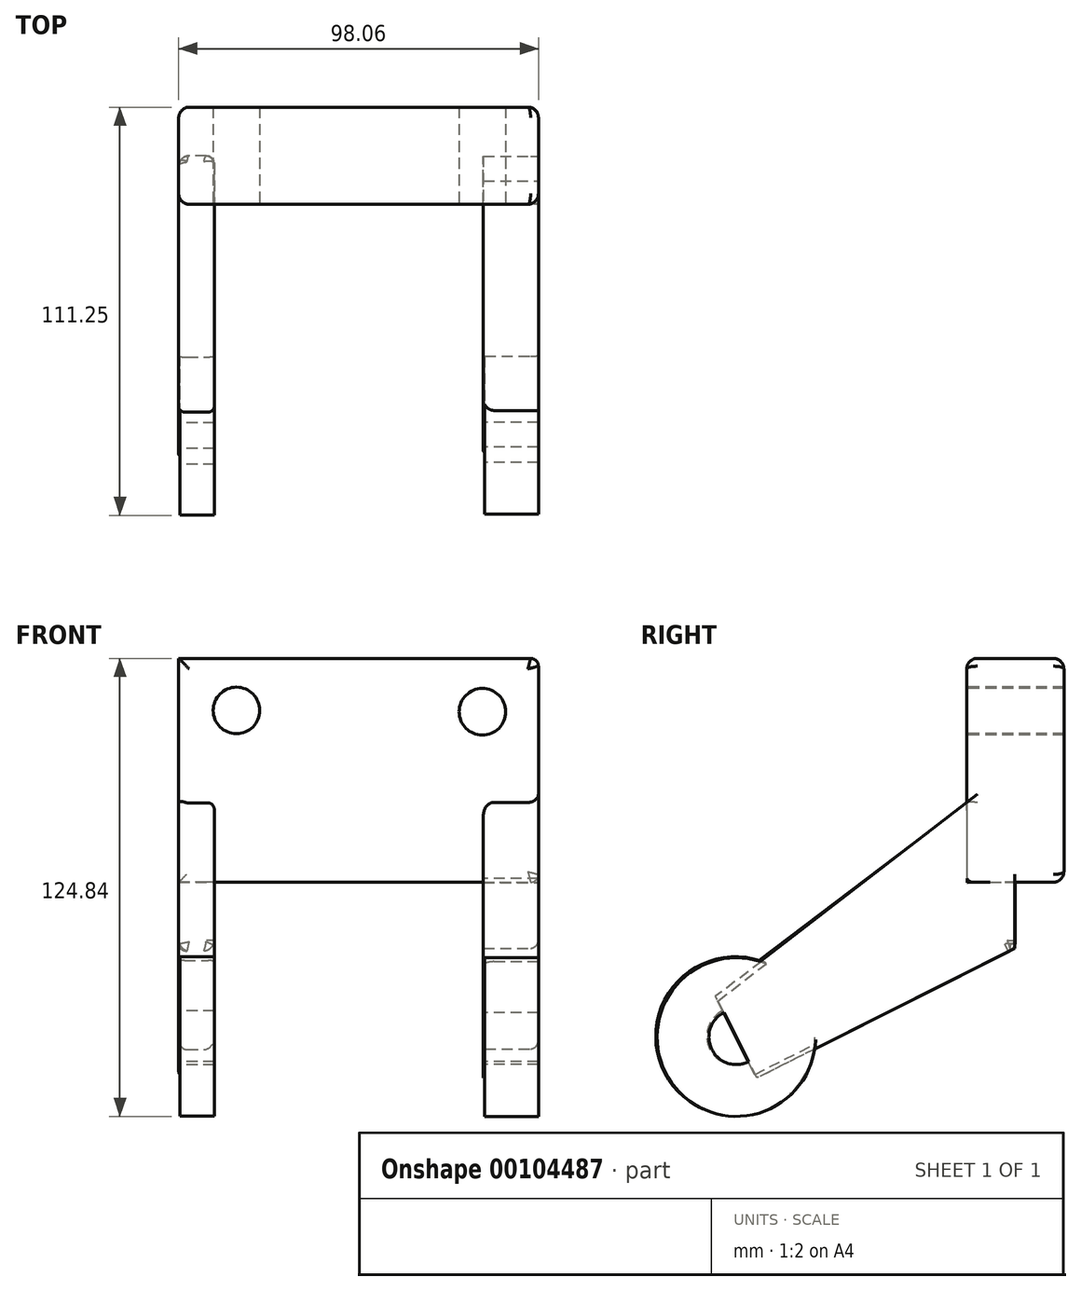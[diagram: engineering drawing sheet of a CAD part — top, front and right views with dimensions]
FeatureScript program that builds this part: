
annotation { "Feature Type Name" : "Feature", "Feature Type Description" : "" }
export const myFeature = defineFeature(function(context is Context, id is Id, definition is map)
    precondition{}
    {
        {
            var Q0;
            Q0=qCreatedBy(makeId("Front.planeOp"),FACE);
            var sketch = newSketch(context, id + "F0", { "sketchPlane" : qUnion([Q0])});
            skLineSegment(sketch, "E0.bottom", {"start": v(-42.16, 33.22) * mm, "end": v(55.9, 33.22) * mm});
            skLineSegment(sketch, "E0.top", {"start": v(-42.16, -27.8) * mm, "end": v(55.9, -27.8) * mm});
            skLineSegment(sketch, "E0.left", {"start": v(-42.16, 33.22) * mm, "end": v(-42.16, -27.8) * mm});
            skLineSegment(sketch, "E0.right", {"start": v(55.9, 33.22) * mm, "end": v(55.9, -27.8) * mm});
            skSolve(sketch);
        }
        {
            var Q0;
            Q0=qSketchRegion(id+"F0",true);
            var Q1;
            Q1=makeQuery(id+"F0.imprint","IMPRINT",FACE,{"disambiguationData":[TD([[makeQuery(id+"F0.imprint","IMPRINT",EDGE,{"derivedFrom":sQuery(id+"F0.wireOp",EDGE,"E0.bottom")}),-1.0]])]});
            extrude(context, id + "F1", {"entities" : qUnion([Q0, Q1]), "depth" : 26.48 * mm});
        }
        {
            var Q0;
            Q0=makeQuery(id+"F1.opExtrude","CAP_FACE",FACE,{"disambiguationData":[OSD([sQuery(id+"F0.wireOp",EDGE,"E0.bottom"),sQuery(id+"F0.wireOp",EDGE,"E0.top"),sQuery(id+"F0.wireOp",EDGE,"E0.left"),sQuery(id+"F0.wireOp",EDGE,"E0.right")])],"isStart":false});
            var sketch = newSketch(context, id + "F2", { "sketchPlane" : qUnion([Q0])});
            skCircle(sketch, "E1", {"center": v(-26.41, 19.02) * mm, "radius": 5.97 * mm});
            skCircle(sketch, "E2", {"center": v(40.64, 18.66) * mm, "radius": 6.46 * mm});
            skSolve(sketch);
        }
        {
            var Q0;
            Q0=sQuery(id+"F2.wireOp",VERTEX,"E1.center");
            var Q1;
            Q1=sQuery(id+"F2.wireOp",VERTEX,"E2.center");
            var Q2;
            Q2=makeQuery(id+"F1.opExtrude","SWEPT_BODY",BODY,{"disambiguationData":[OSD([sQuery(id+"F0.wireOp",EDGE,"E0.bottom"),sQuery(id+"F0.wireOp",EDGE,"E0.top"),sQuery(id+"F0.wireOp",EDGE,"E0.left"),sQuery(id+"F0.wireOp",EDGE,"E0.right")])]});
            hole(context, id + "F3", {"style" : HoleStyle.SIMPLE, "endStyle" : HoleEndStyle.THROUGH, "holeDiameter" : 12.7 * mm, "locations" : qUnion([Q0, Q1]), "scope" : qUnion([Q2]), "isTappedThrough" : true});
        }
        {
            var Q0;
            Q0=makeQuery(id+"F1.opExtrude","SWEPT_FACE",FACE,{"disambiguationData":[OSD([sQuery(id+"F0.wireOp",EDGE,"E0.right")])]});
            var sketch = newSketch(context, id + "F4", { "sketchPlane" : qUnion([Q0])});
            skSolve(sketch);
        }
        {
            var Q0;
            Q0=makeQuery(id+"F1.opExtrude","SWEPT_FACE",FACE,{"disambiguationData":[OSD([sQuery(id+"F0.wireOp",EDGE,"E0.left")])]});
            var sketch = newSketch(context, id + "F5", { "sketchPlane" : qUnion([Q0])});
            skLineSegment(sketch, "E3", {"start": v(13.24, -27.8) * mm, "end": v(13.24, -45.74) * mm});
            skLineSegment(sketch, "E4", {"start": v(13.24, -45.74) * mm, "end": v(83.77, -81.27) * mm});
            skLineSegment(sketch, "E5", {"start": v(83.77, -81.27) * mm, "end": v(95.33, -58.32) * mm});
            skLineSegment(sketch, "E6", {"start": v(95.33, -58.32) * mm, "end": v(26.48, -6.2) * mm});
            skLineSegment(sketch, "E7", {"start": v(26.48, -6.2) * mm, "end": v(26.48, -27.8) * mm});
            skLineSegment(sketch, "E8", {"start": v(26.48, -27.8) * mm, "end": v(13.24, -27.8) * mm});
            skSolve(sketch);
        }
        {
            var Q0;
            Q0=makeQuery(id+"F5.imprint","IMPRINT",FACE,{"disambiguationData":[TD([[makeQuery(id+"F5.imprint","IMPRINT",EDGE,{"derivedFrom":sQuery(id+"F5.wireOp",EDGE,"E3")}),1.0]])]});
            extrude(context, id + "F6", {"entities" : qUnion([Q0]), "operationType" : NewBodyOperationType.ADD, "oppositeDirection" : true, "depth" : 9.71 * mm});
        }
        {
            var Q0;
            {var subQ0=sQuery(id+"F0.wireOp",EDGE,"E0.right");Q0=makeQuery(id+"F4.imprint","IMPRINT",FACE,{"disambiguationData":[TD([[makeQuery(id+"F4.imprint","IMPRINT",EDGE,{"derivedFrom":makeQuery(id+"F1.opExtrude","CAP_EDGE",EDGE,{"disambiguationData":[OSD([subQ0])],"isStart":true})}),-1.0]])]});}
            var sketch = newSketch(context, id + "F7", { "sketchPlane" : qUnion([Q0])});
            skLineSegment(sketch, "E9", {"start": v(-13.36, -27.68) * mm, "end": v(-13.36, -45.8) * mm});
            skLineSegment(sketch, "E10", {"start": v(-13.36, -45.8) * mm, "end": v(-83.68, -81.16) * mm});
            skLineSegment(sketch, "E11", {"start": v(-83.68, -81.16) * mm, "end": v(-94.9, -58.86) * mm});
            skLineSegment(sketch, "E12", {"start": v(-94.9, -58.86) * mm, "end": v(-26.36, -5.95) * mm});
            skLineSegment(sketch, "E13", {"start": v(-26.36, -5.95) * mm, "end": v(-26.36, -27.9) * mm});
            skLineSegment(sketch, "E14", {"start": v(-26.36, -27.9) * mm, "end": v(-13.36, -27.68) * mm});
            skSolve(sketch);
        }
        {
            var Q0;
            {var subQ10=sQuery(id+"F7.wireOp",EDGE,"E10");Q0=makeQuery(id+"F7.imprint","IMPRINT",FACE,{"disambiguationData":[TD([[makeQuery(id+"F7.imprint","IMPRINT",EDGE,{"derivedFrom":subQ10}),-1.0]])]});}
            extrude(context, id + "F8", {"entities" : qUnion([Q0]), "operationType" : NewBodyOperationType.ADD, "oppositeDirection" : true, "depth" : 15.02 * mm});
        }
        {
            var Q0;
            Q0=makeQuery(id+"F6.opExtrude","CAP_FACE",FACE,{"disambiguationData":[OSD([sQuery(id+"F5.wireOp",EDGE,"E3"),sQuery(id+"F5.wireOp",EDGE,"E4"),sQuery(id+"F5.wireOp",EDGE,"E5"),sQuery(id+"F5.wireOp",EDGE,"E6"),sQuery(id+"F5.wireOp",EDGE,"E7"),sQuery(id+"F5.wireOp",EDGE,"E8")])],"isStart":false});
            var sketch = newSketch(context, id + "F9", { "sketchPlane" : qUnion([Q0])});
            skCircle(sketch, "E15", {"center": v(-89.55, -69.8) * mm, "radius": 21.7 * mm});
            skSolve(sketch);
        }
        {
            var Q0;
            {var subQ0=sQuery(id+"F0.wireOp",EDGE,"E0.right");Q0=makeQuery(id+"F8.boolean.opBoolean","MERGE",FACE,{"derivedFrom":[makeQuery(id+"F1.opExtrude","SWEPT_FACE",FACE,{"disambiguationData":[OSD([subQ0])]}),makeQuery(id+"F8.opExtrude","CAP_FACE",FACE,{"disambiguationData":[OSD([sQuery(id+"F0.wireOp",EDGE,"E0.top"),subQ0,sQuery(id+"F7.wireOp",EDGE,"E9"),sQuery(id+"F7.wireOp",EDGE,"E10"),sQuery(id+"F7.wireOp",EDGE,"E11"),sQuery(id+"F7.wireOp",EDGE,"E12"),sQuery(id+"F7.wireOp",EDGE,"E13"),sQuery(id+"F7.wireOp",EDGE,"E14")])],"isStart":true})]});}
            var sketch = newSketch(context, id + "F10", { "sketchPlane" : qUnion([Q0])});
            skCircle(sketch, "E16", {"center": v(-89.29, -70) * mm, "radius": 21.61 * mm});
            skSolve(sketch);
        }
        {
            var Q0;
            {var subQ5=makeQuery(id+"F8.opExtrude","CAP_EDGE",EDGE,{"disambiguationData":[OSD([sQuery(id+"F7.wireOp",EDGE,"E11")])],"isStart":true});Q0=makeQuery(id+"F10.imprint","IMPRINT",FACE,{"disambiguationData":[TD([[makeQuery(id+"F10.imprint","IMPRINT",EDGE,{"derivedFrom":subQ5}),1.0]])]});}
            extrude(context, id + "F11", {"entities" : qUnion([Q0]), "operationType" : NewBodyOperationType.ADD, "oppositeDirection" : true, "depth" : 14.62 * mm});
        }
        {
            var Q0;
            {var subQ5=makeQuery(id+"F6.opExtrude","CAP_EDGE",EDGE,{"disambiguationData":[OSD([sQuery(id+"F5.wireOp",EDGE,"E5")])],"isStart":false});Q0=makeQuery(id+"F9.imprint","IMPRINT",FACE,{"disambiguationData":[TD([[makeQuery(id+"F9.imprint","IMPRINT",EDGE,{"derivedFrom":subQ5}),1.0]])]});}
            extrude(context, id + "F12", {"entities" : qUnion([Q0]), "operationType" : NewBodyOperationType.ADD, "oppositeDirection" : true, "depth" : 9.44 * mm});
        }
        {
            var Q0;
            Q0=makeQuery(id+"F11.opExtrude","CAP_FACE",FACE,{"disambiguationData":[OSD([sQuery(id+"F7.wireOp",EDGE,"E10"),sQuery(id+"F7.wireOp",EDGE,"E11"),sQuery(id+"F7.wireOp",EDGE,"E12"),sQuery(id+"F10.wireOp",EDGE,"E16")])],"isStart":false});
            var sketch = newSketch(context, id + "F13", { "sketchPlane" : qUnion([Q0])});
            skCircle(sketch, "E17", {"center": v(89.29, -70) * mm, "radius": 7.5 * mm});
            skSolve(sketch);
        }
        {
            var Q0;
            Q0=makeQuery(id+"F12.opExtrude","CAP_FACE",FACE,{"disambiguationData":[OSD([sQuery(id+"F5.wireOp",EDGE,"E4"),sQuery(id+"F5.wireOp",EDGE,"E5"),sQuery(id+"F5.wireOp",EDGE,"E6"),sQuery(id+"F9.wireOp",EDGE,"E15")])],"isStart":false});
            var sketch = newSketch(context, id + "F14", { "sketchPlane" : qUnion([Q0])});
            skCircle(sketch, "E18", {"center": v(89.55, -69.8) * mm, "radius": 7.77 * mm});
            skSolve(sketch);
        }
        {
            var Q0;
            {var subQ0=sQuery(id+"F14.wireOp",EDGE,"E18");var subQ1=makeQuery(id+"F12.opExtrude","CAP_EDGE",EDGE,{"disambiguationData":[OSD([sQuery(id+"F5.wireOp",EDGE,"E5")])],"isStart":false});var subQ2=makeQuery(id+"F14.imprint","INTERSECT",VERTEX,{"disambiguationData":[OD(0.0)],"derivedFrom":[subQ1,subQ0]});Q0=makeQuery(id+"F14.imprint","IMPRINT",FACE,{"disambiguationData":[TD([[makeQuery(id+"F14.imprint","IMPRINT",EDGE,{"disambiguationData":[TD([[subQ2,-1.0]])],"derivedFrom":subQ0}),1.0]])]});}
            var sketch = newSketch(context, id + "F15", { "sketchPlane" : qUnion([Q0])});
            skSolve(sketch);
        }
        {
            var Q0;
            Q0=qSketchRegion(id+"F15",true);
            var Q1;
            {var subQ0=sQuery(id+"F14.wireOp",EDGE,"E18");var subQ1=makeQuery(id+"F12.opExtrude","CAP_EDGE",EDGE,{"disambiguationData":[OSD([sQuery(id+"F5.wireOp",EDGE,"E5")])],"isStart":false});var subQ2=makeQuery(id+"F14.imprint","INTERSECT",VERTEX,{"disambiguationData":[OD(0.0)],"derivedFrom":[subQ1,subQ0]});Q1=makeQuery(id+"F14.imprint","IMPRINT",FACE,{"disambiguationData":[TD([[makeQuery(id+"F14.imprint","IMPRINT",EDGE,{"disambiguationData":[TD([[subQ2,-1.0]])],"derivedFrom":subQ0}),1.0]])]});}
            extrude(context, id + "F16", {"entities" : qUnion([Q0, Q1]), "operationType" : NewBodyOperationType.REMOVE, "oppositeDirection" : true, "depth" : 25.4 * mm});
        }
        {
            var Q0;
            {var subQ0=sQuery(id+"F13.wireOp",EDGE,"E17");var subQ1=makeQuery(id+"F11.opExtrude","CAP_EDGE",EDGE,{"disambiguationData":[OSD([sQuery(id+"F7.wireOp",EDGE,"E11")])],"isStart":false});var subQ2=makeQuery(id+"F13.imprint","INTERSECT",VERTEX,{"disambiguationData":[OD(0.0)],"derivedFrom":[subQ1,subQ0]});Q0=makeQuery(id+"F13.imprint","IMPRINT",FACE,{"disambiguationData":[TD([[makeQuery(id+"F13.imprint","IMPRINT",EDGE,{"disambiguationData":[TD([[subQ2,-1.0]])],"derivedFrom":subQ0}),1.0]])]});}
            extrude(context, id + "F17", {"entities" : qUnion([Q0]), "operationType" : NewBodyOperationType.REMOVE, "oppositeDirection" : true, "depth" : 25.4 * mm});
        }
        {
            var Q0;
            {var subQ0=sQuery(id+"F14.wireOp",EDGE,"E18");var subQ1=makeQuery(id+"F12.opExtrude","CAP_EDGE",EDGE,{"disambiguationData":[OSD([sQuery(id+"F5.wireOp",EDGE,"E5")])],"isStart":false});var subQ2=makeQuery(id+"F14.imprint","INTERSECT",VERTEX,{"disambiguationData":[OD(0.0)],"derivedFrom":[subQ1,subQ0]});Q0=makeQuery(id+"F15.imprint","IMPRINT",FACE,{"disambiguationData":[TD([[makeQuery(id+"F15.imprint","IMPRINT",EDGE,{"derivedFrom":makeQuery(id+"F14.imprint","IMPRINT",EDGE,{"disambiguationData":[TD([[subQ2,-1.0]])],"derivedFrom":subQ0})}),1.0]])]});}
            extrude(context, id + "F18", {"entities" : qUnion([Q0]), "operationType" : NewBodyOperationType.REMOVE, "oppositeDirection" : true, "depth" : 23.17 * mm});
        }
        {
            var Q0;
            Q0=makeQuery(id+"F1.opExtrude","CAP_EDGE",EDGE,{"disambiguationData":[OSD([sQuery(id+"F0.wireOp",EDGE,"E0.bottom")])],"isStart":false});
            var Q1;
            Q1=makeQuery(id+"F1.opExtrude","CAP_EDGE",EDGE,{"disambiguationData":[OSD([sQuery(id+"F0.wireOp",EDGE,"E0.left")])],"isStart":false});
            var Q2;
            Q2=makeQuery(id+"F1.opExtrude","CAP_EDGE",EDGE,{"disambiguationData":[OSD([sQuery(id+"F0.wireOp",EDGE,"E0.right")])],"isStart":false});
            var Q3;
            Q3=makeQuery(id+"F8.opExtrude","SWEPT_EDGE",EDGE,{"disambiguationData":[OSD([sQuery(id+"F0.wireOp",EDGE,"E0.right"),sQuery(id+"F7.wireOp",EDGE,"E12")])]});
            var Q4;
            Q4=makeQuery(id+"F8.opExtrude","CAP_EDGE",EDGE,{"disambiguationData":[OSD([sQuery(id+"F7.wireOp",EDGE,"E12")])],"isStart":false});
            fillet(context, id + "F19", {"entities" : qUnion([Q0, Q1, Q2, Q3, Q4]), "radius" : 2.87 * mm, "tangentPropagation" : true, "allowEdgeOverflow" : false});
        }
        {
            var Q0;
            Q0=makeQuery(id+"F1.opExtrude","CAP_EDGE",EDGE,{"disambiguationData":[OSD([sQuery(id+"F0.wireOp",EDGE,"E0.top")])],"isStart":false});
            var Q1;
            Q1=makeQuery(id+"F6.opExtrude","CAP_EDGE",EDGE,{"disambiguationData":[OSD([sQuery(id+"F5.wireOp",EDGE,"E6")])],"isStart":false});
            var Q2;
            Q2=makeQuery(id+"F6.opExtrude","CAP_EDGE",EDGE,{"disambiguationData":[OSD([sQuery(id+"F5.wireOp",EDGE,"E6")])],"isStart":true});
            fillet(context, id + "F20", {"entities" : qUnion([Q0, Q1, Q2]), "radius" : 1.58 * mm, "tangentPropagation" : true, "allowEdgeOverflow" : false});
        }
        {
            var Q0;
            Q0=makeQuery(id+"F1.opExtrude","SWEPT_EDGE",EDGE,{"disambiguationData":[OSD([sQuery(id+"F0.wireOp",EDGE,"E0.bottom"),sQuery(id+"F0.wireOp",EDGE,"E0.right")])]});
            var Q1;
            Q1=makeQuery(id+"F6.opExtrude","CAP_EDGE",EDGE,{"disambiguationData":[OSD([sQuery(id+"F5.wireOp",EDGE,"E3")])],"isStart":false});
            var Q2;
            {var subQ0=sQuery(id+"F7.wireOp",EDGE,"E9");var subQ1=sQuery(id+"F0.wireOp",EDGE,"E0.right");var subQ2=sQuery(id+"F0.wireOp",EDGE,"E0.top");Q2=makeQuery(id+"F8.boolean.opBoolean","SPLIT",EDGE,{"disambiguationData":[TD([makeQuery(id+"F8.opExtrude","SWEPT_FACE",FACE,{"disambiguationData":[OSD([subQ0])]})])],"derivedFrom":makeQuery(id+"F1.opExtrude","SWEPT_EDGE",EDGE,{"disambiguationData":[OSD([subQ2,subQ1])]})});}
            var Q3;
            Q3=makeQuery(id+"F8.opExtrude","CAP_EDGE",EDGE,{"disambiguationData":[OSD([sQuery(id+"F7.wireOp",EDGE,"E10")])],"isStart":true});
            fillet(context, id + "F21", {"entities" : qUnion([Q0, Q1, Q2, Q3]), "radius" : 2.13 * mm, "tangentPropagation" : true, "allowEdgeOverflow" : false});
        }
        {
            var Q0;
            Q0=makeQuery(id+"F1.opExtrude","CAP_EDGE",EDGE,{"disambiguationData":[OSD([sQuery(id+"F0.wireOp",EDGE,"E0.left")])],"isStart":true});
            var Q1;
            Q1=makeQuery(id+"F1.opExtrude","CAP_EDGE",EDGE,{"disambiguationData":[OSD([sQuery(id+"F0.wireOp",EDGE,"E0.top")])],"isStart":true});
            var Q2;
            Q2=makeQuery(id+"F6.opExtrude","CAP_EDGE",EDGE,{"disambiguationData":[OSD([sQuery(id+"F5.wireOp",EDGE,"E3")])],"isStart":true});
            var Q3;
            Q3=makeQuery(id+"F6.opExtrude","SWEPT_EDGE",EDGE,{"disambiguationData":[OSD([sQuery(id+"F5.wireOp",EDGE,"E3"),sQuery(id+"F5.wireOp",EDGE,"E4")])]});
            fillet(context, id + "F22", {"entities" : qUnion([Q0, Q1, Q2, Q3]), "radius" : 2.87 * mm, "tangentPropagation" : true, "allowEdgeOverflow" : false});
        }
        {
            var Q0;
            Q0=makeQuery(id+"F6.opExtrude","CAP_EDGE",EDGE,{"disambiguationData":[OSD([sQuery(id+"F5.wireOp",EDGE,"E4")])],"isStart":true});
            fillet(context, id + "F23", {"entities" : qUnion([Q0]), "radius" : 2.27 * mm, "tangentPropagation" : true, "allowEdgeOverflow" : false});
        }
    });
